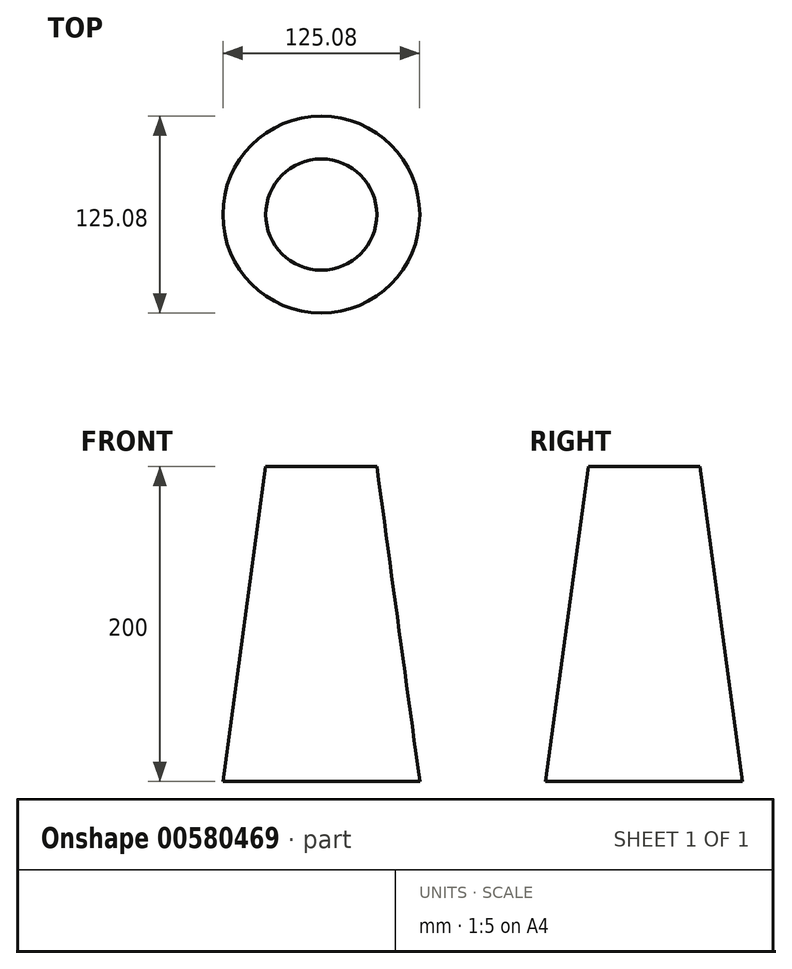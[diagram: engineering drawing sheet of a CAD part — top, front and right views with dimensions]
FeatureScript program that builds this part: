
annotation { "Feature Type Name" : "Feature", "Feature Type Description" : "" }
export const myFeature = defineFeature(function(context is Context, id is Id, definition is map)
    precondition{}
    {
        {
            var Q0;
            Q0=qCreatedBy(makeId("Top.planeOp"),FACE);
            var sketch = newSketch(context, id + "F0", { "sketchPlane" : qUnion([Q0])});
            skCircle(sketch, "E0", {"center": v(0, 0) * mm, "radius": 35.27 * mm});
            skSolve(sketch);
        }
        {
            var Q0;
            Q0=qCreatedBy(makeId("Top.planeOp"),FACE);
            cPlane(context, id + "F1", {"entities" : qUnion([Q0]), "cplaneType" : CPlaneType.OFFSET, "offset" : 200 * mm, "oppositeDirection" : true, "width" : 150 * mm, "height" : 150 * mm});
        }
        {
            var Q0;
            Q0=qCreatedBy(id+"F1.planeOp",FACE);
            var sketch = newSketch(context, id + "F2", { "sketchPlane" : qUnion([Q0])});
            skCircle(sketch, "E1", {"center": v(0, 0) * mm, "radius": 62.54 * mm});
            skSolve(sketch);
        }
        {
            var Q0;
            Q0=makeQuery(id+"F0.imprint","IMPRINT",FACE,{"disambiguationData":[TD([[makeQuery(id+"F0.imprint","IMPRINT",EDGE,{"derivedFrom":sQuery(id+"F0.wireOp",EDGE,"E0")}),1.0]])]});
            var Q1;
            Q1=makeQuery(id+"F2.imprint","IMPRINT",FACE,{"disambiguationData":[TD([[makeQuery(id+"F2.imprint","IMPRINT",EDGE,{"derivedFrom":sQuery(id+"F2.wireOp",EDGE,"E1")}),1.0]])]});
            loft(context, id + "F3", {"sheetProfilesArray" : [{ "sheetProfileEntities" : qUnion([Q0]) }, { "sheetProfileEntities" : qUnion([Q1]) }]});
        }
    });
